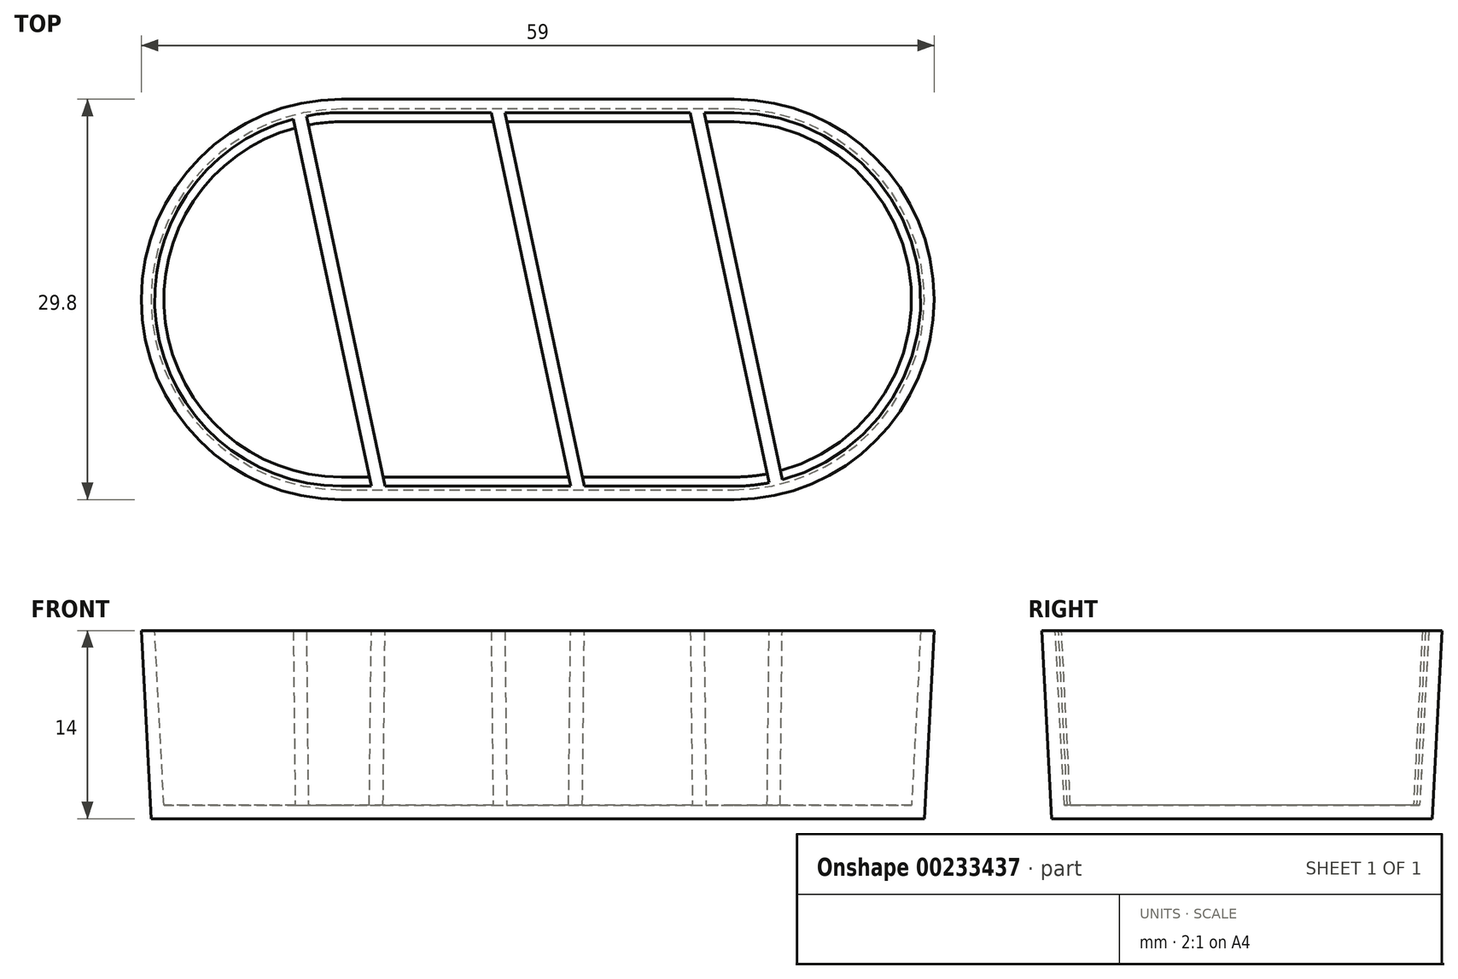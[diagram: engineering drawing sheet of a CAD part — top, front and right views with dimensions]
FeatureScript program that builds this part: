
annotation { "Feature Type Name" : "Feature", "Feature Type Description" : "" }
export const myFeature = defineFeature(function(context is Context, id is Id, definition is map)
    precondition{}
    {
        {
            var Q0;
            Q0=qCreatedBy(makeId("Top.planeOp"),FACE);
            var sketch = newSketch(context, id + "F0", { "sketchPlane" : qUnion([Q0])});
            skArc(sketch, "E0", {"start": v(-14.6, 14.9) * mm, "mid": v(-29.5, 0) * mm, "end": v(-14.6, -14.9) * mm});
            skArc(sketch, "E1", {"start": v(14.6, -14.9) * mm, "mid": v(29.5, 0) * mm, "end": v(14.6, 14.9) * mm});
            skLineSegment(sketch, "E2", {"start": v(-14.6, 14.9) * mm, "end": v(14.6, 14.9) * mm});
            skLineSegment(sketch, "E3", {"start": v(-14.6, -14.9) * mm, "end": v(14.6, -14.9) * mm});
            skLineSegment(sketch, "E4", {"start": v(0, 14.9) * mm, "end": v(0, -14.9) * mm, "construction": true});
            skSolve(sketch);
        }
        {
            var Q0;
            Q0 = qSketchRegion(id + "F0", true);
            extrude(context, id + "F1", {"entities" : qUnion([Q0]), "oppositeDirection" : true, "depth" : 14 * mm, "hasDraft" : true, "draftAngle" : 3 * degree, "draftPullDirection" : true});
        }
        {
            var Q0;
            Q0=makeQuery(id+"F1.opExtrude","CAP_FACE",FACE,{"disambiguationData":[OSD([sQuery(id+"F0.wireOp",EDGE,"E0"),sQuery(id+"F0.wireOp",EDGE,"E1"),sQuery(id+"F0.wireOp",EDGE,"E2"),sQuery(id+"F0.wireOp",EDGE,"E3")])],"isStart":true});
            shell(context, id + "F2", {"entities" : qUnion([Q0]), "thickness" : 1 * mm});
        }
        {
            var Q0;
            Q0=makeQuery(id+"F2.opShell","OFFSET_FACE",FACE,{"disambiguationData":[OSD([sQuery(id+"F0.wireOp",EDGE,"E0"),sQuery(id+"F0.wireOp",EDGE,"E1"),sQuery(id+"F0.wireOp",EDGE,"E2"),sQuery(id+"F0.wireOp",EDGE,"E3")])]});
            var sketch = newSketch(context, id + "F3", { "sketchPlane" : qUnion([Q0])});
            skLineSegment(sketch, "E5", {"start": v(-2.8, 13.22) * mm, "end": v(2.8, -13.22) * mm, "construction": true});
            skLineSegment(sketch, "E6", {"start": v(0, 0) * mm, "end": v(0, 5.64) * mm, "construction": true});
            skLineSegment(sketch, "E7.0", {"start": v(-3.47, 13.9) * mm, "end": v(2.44, -13.9) * mm});
            skLineSegment(sketch, "E8.0", {"start": v(-2.44, 13.9) * mm, "end": v(3.47, -13.9) * mm});
            skLineSegment(sketch, "E9", {"start": v(-3.47, 13.9) * mm, "end": v(-2.44, 13.9) * mm});
            skLineSegment(sketch, "E10", {"start": v(2.44, -13.9) * mm, "end": v(3.47, -13.9) * mm});
            skLineSegment(sketch, "E11.0", {"start": v(-17, 10.2) * mm, "end": v(-11.37, -16.23) * mm, "construction": true});
            skLineSegment(sketch, "E12.0", {"start": v(11.37, 16.23) * mm, "end": v(17, -10.2) * mm, "construction": true});
            skLineSegment(sketch, "E13.0", {"start": v(-18.19, 13.43) * mm, "end": v(-12.38, -13.9) * mm});
            skLineSegment(sketch, "E14.0", {"start": v(-17.21, 13.65) * mm, "end": v(-11.36, -13.9) * mm});
            skLineSegment(sketch, "E15.0", {"start": v(11.36, 13.9) * mm, "end": v(17.21, -13.65) * mm});
            skLineSegment(sketch, "E16.0", {"start": v(12.38, 13.9) * mm, "end": v(18.19, -13.43) * mm});
            skLineSegment(sketch, "E17", {"start": v(-12.38, -13.9) * mm, "end": v(-11.36, -13.9) * mm});
            skLineSegment(sketch, "E18", {"start": v(11.36, 13.9) * mm, "end": v(12.38, 13.9) * mm});
            skArc(sketch, "E19.0", {"start": v(-17.21, 13.65) * mm, "mid": v(-17.7, 13.55) * mm, "end": v(-18.19, 13.43) * mm});
            skPoint(sketch, "E20.orphan", {"position": v(-14.6, 13.9) * mm});
            skPoint(sketch, "E21.orphan", {"position": v(-14.6, -13.9) * mm});
            skArc(sketch, "E22.0", {"start": v(17.21, -13.65) * mm, "mid": v(17.7, -13.55) * mm, "end": v(18.19, -13.43) * mm});
            skPoint(sketch, "E23.orphan", {"position": v(14.6, -13.9) * mm});
            skPoint(sketch, "E24.orphan", {"position": v(14.6, 13.9) * mm});
            skSolve(sketch);
        }
        {
            var Q0;
            Q0 = qSketchRegion(id + "F3", true);
            var Q1;
            Q1=makeQuery(id+"F1.opExtrude","CAP_FACE",FACE,{"disambiguationData":[OSD([sQuery(id+"F0.wireOp",EDGE,"E0"),sQuery(id+"F0.wireOp",EDGE,"E1"),sQuery(id+"F0.wireOp",EDGE,"E2"),sQuery(id+"F0.wireOp",EDGE,"E3")])],"isStart":true});
            extrude(context, id + "F4", {"entities" : qUnion([Q0]), "operationType" : NewBodyOperationType.ADD, "endBound" : BoundingType.UP_TO_SURFACE, "endBoundEntityFace" : qUnion([Q1]), "depth" : 25 * mm});
        }
    });
